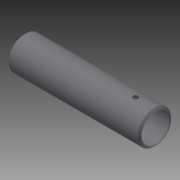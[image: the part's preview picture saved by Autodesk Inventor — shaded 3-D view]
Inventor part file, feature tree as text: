
AUTODESK INVENTOR PART (.ipt)
format: ipt  version: 2014 (Build 180170000, 170)  size: 134,656 bytes
history: native  units: in
note: dims shown in document units (in); Inventor stores cm internally (conversion verified against a paired STEP export)
features: other x56, revolve x2, sketch x2
ambient origin geometry x8: Origin, YZ Plane, XZ Plane, XY Plane, X Axis, Y Axis, Z Axis, Center Point
bodies: Solid1 (feature_tree)
feature tree (60):
  revolve  "Revolution1"  Angle=360.0deg
  revolve  "Revolution2"  [1 undecoded]
  other  "o1_XY"
  other  "o1_YZ"
  other  "o1_ZX"
  other  "o1_X"
  other  "o1_Y"
  other  "o1_Z"
  other  "o1_Center"
  other  "o2_XY"
  other  "o2_YZ"
  other  "o2_ZX"
  other  "o2_X"
  other  "o2_Y"
  other  "o2_Z"
  other  "o2_Center"
  other  "t1_XY"
  other  "t1_YZ"
  other  "t1_ZX"
  other  "t1_X"
  other  "t1_Y"
  other  "t1_Z"
  other  "t1_Center"
  other  "t2_XY"
  other  "t2_YZ"
  other  "t2_ZX"
  other  "t2_X"
  other  "t2_Y"
  other  "t2_Z"
  other  "t2_Center"
  other  "t3_XY"
  other  "t3_YZ"
  other  "t3_ZX"
  other  "t3_X"
  other  "t3_Y"
  other  "t3_Z"
  other  "t3_Center"
  other  "t4_XY"
  other  "t4_YZ"
  other  "t4_ZX"
  other  "t4_X"
  other  "t4_Y"
  other  "t4_Z"
  other  "t4_Center"
  other  "tube1_XY"
  other  "tube1_YZ"
  other  "tube1_ZX"
  other  "tube1_X"
  other  "tube1_Y"
  other  "tube1_Z"
  other  "tube1_Center"
  other  "tube2_XY"
  other  "tube2_YZ"
  other  "tube2_ZX"
  other  "tube2_X"
  other  "tube2_Y"
  other  "tube2_Z"
  other  "tube2_Center"
  sketch  "Sketch_5"
  sketch  "Sketch_1"  dims[d0=360.0deg d1=360.0deg]
note: 1 required parameter value undecoded (feature->parameter linkage not recoverable at this tier; creation-order binding heuristic only, values carry confidence <= 0.55)
